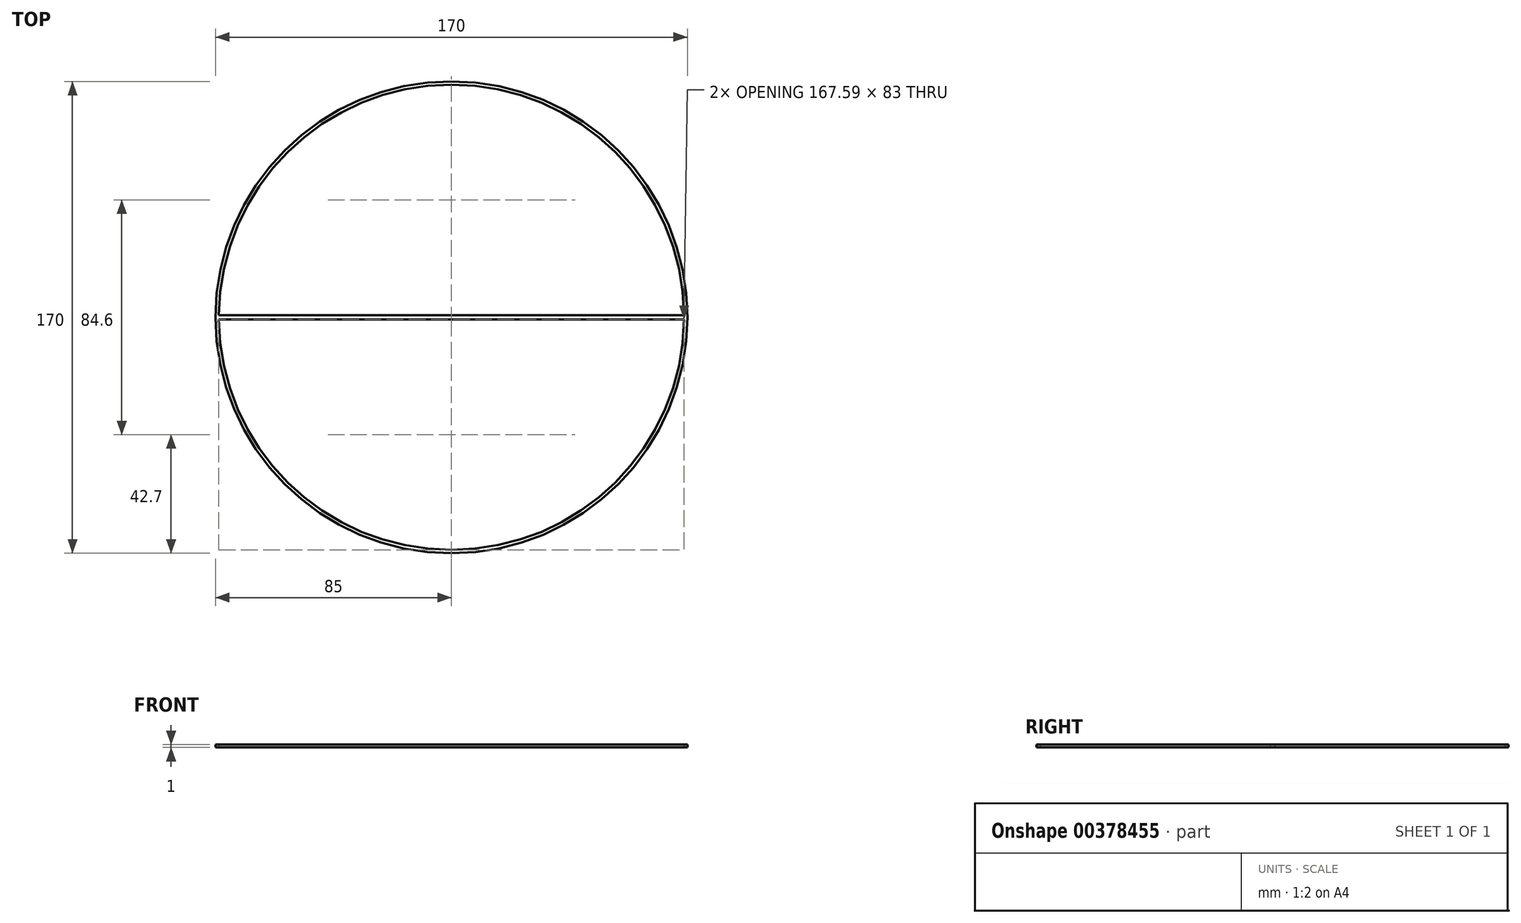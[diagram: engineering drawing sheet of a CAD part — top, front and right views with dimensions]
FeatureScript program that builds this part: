
annotation { "Feature Type Name" : "Feature", "Feature Type Description" : "" }
export const myFeature = defineFeature(function(context is Context, id is Id, definition is map)
    precondition{}
    {
        {
            var Q0;
            Q0=qCreatedBy(makeId("Top.planeOp"),FACE);
            var sketch = newSketch(context, id + "F0", { "sketchPlane" : qUnion([Q0])});
            skCircle(sketch, "E0", {"center": v(0, 0) * mm, "radius": 85 * mm});
            skArc(sketch, "E1", {"start": v(-83.8, -0.8) * mm, "mid": v(0, -83.8) * mm, "end": v(83.8, -0.8) * mm});
            skLineSegment(sketch, "E2.bottom", {"start": v(-83.8, 0.8) * mm, "end": v(83.8, 0.8) * mm});
            skLineSegment(sketch, "E2.top", {"start": v(-83.8, -0.8) * mm, "end": v(83.8, -0.8) * mm});
            skArc(sketch, "E3.trimOffspring", {"start": v(83.8, 0.8) * mm, "mid": v(0, 83.8) * mm, "end": v(-83.8, 0.8) * mm});
            skSolve(sketch);
        }
        {
            var Q0;
            Q0=makeQuery(id+"F0.imprint","IMPRINT",FACE,{"disambiguationData":[TD([[makeQuery(id+"F0.imprint","IMPRINT",EDGE,{"derivedFrom":sQuery(id+"F0.wireOp",EDGE,"E0")}),1.0]])]});
            extrude(context, id + "F1", {"entities" : qUnion([Q0]), "depth" : 1 * mm});
        }
    });
